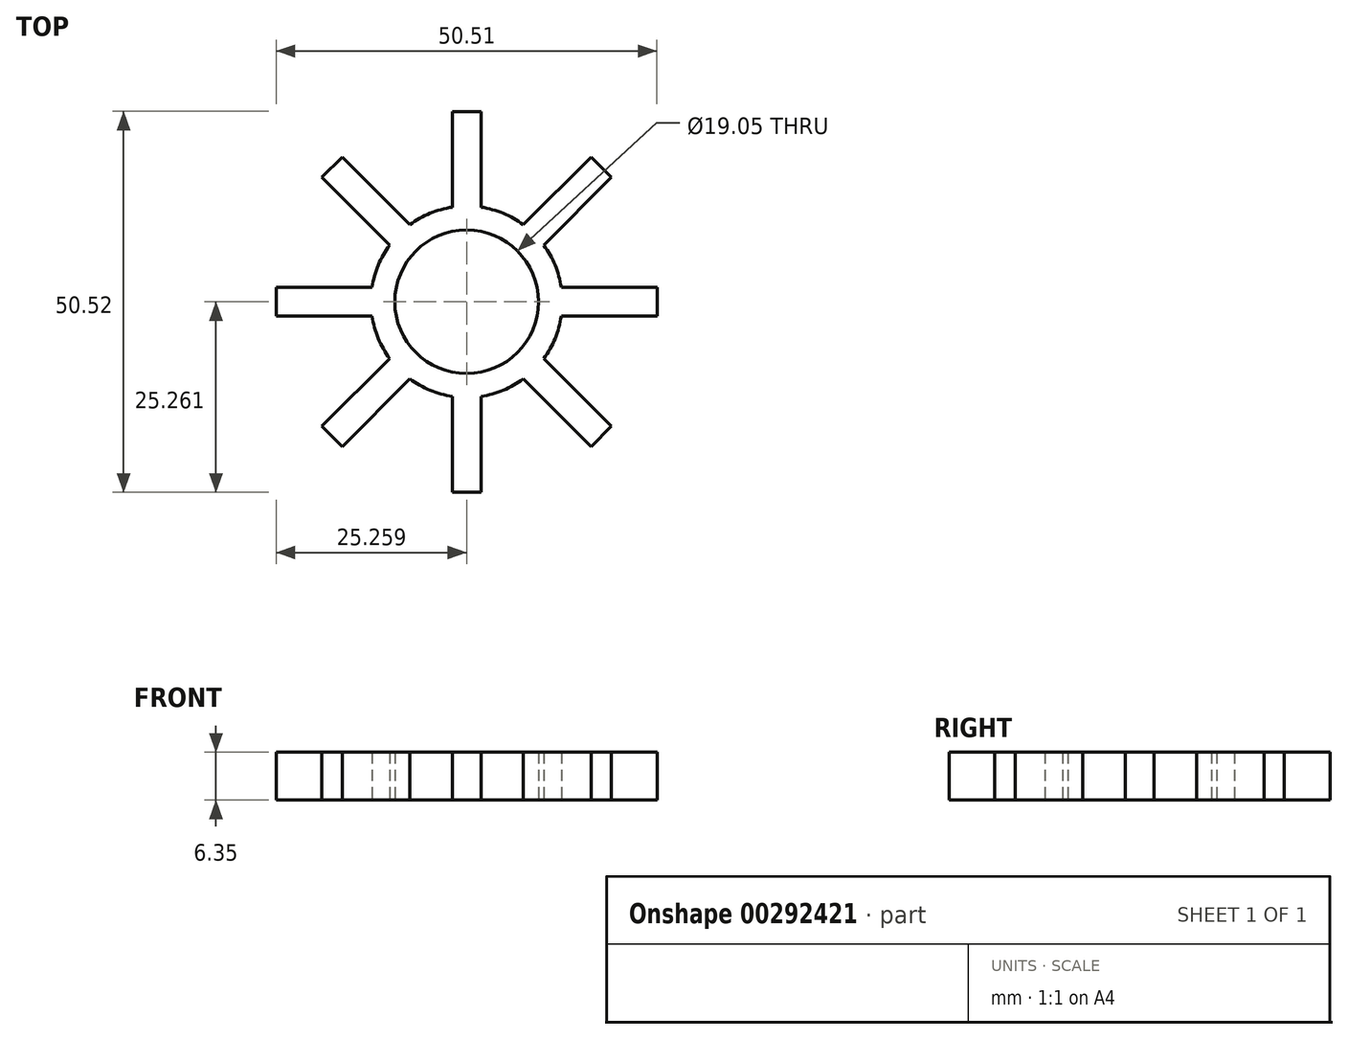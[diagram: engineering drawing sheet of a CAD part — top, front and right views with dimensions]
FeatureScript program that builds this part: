
annotation { "Feature Type Name" : "Feature", "Feature Type Description" : "" }
export const myFeature = defineFeature(function(context is Context, id is Id, definition is map)
    precondition{}
    {
        {
            var Q0;
            Q0=qCreatedBy(makeId("Top.planeOp"),FACE);
            var sketch = newSketch(context, id + "F0", { "sketchPlane" : qUnion([Q0])});
            skCircle(sketch, "E0", {"center": v(-10.94, 8.06) * mm, "radius": 9.53 * mm});
            skCircle(sketch, "E1", {"center": v(-10.94, 8.06) * mm, "radius": 12.7 * mm});
            skLineSegment(sketch, "E2.bottom", {"start": v(-12.85, 20.62) * mm, "end": v(-9.04, 20.62) * mm});
            skLineSegment(sketch, "E2.top", {"start": v(-12.85, 33.32) * mm, "end": v(-9.04, 33.32) * mm});
            skLineSegment(sketch, "E2.left", {"start": v(-12.85, 20.62) * mm, "end": v(-12.85, 33.32) * mm});
            skLineSegment(sketch, "E2.right", {"start": v(-9.04, 20.62) * mm, "end": v(-9.04, 33.32) * mm});
            skSolve(sketch);
        }
        {
            var Q0;
            Q0 = qSketchRegion(id + "F0", true);
            extrude(context, id + "F1", {"entities" : qUnion([Q0]), "depth" : 6.35 * mm, "offsetDistance" : 25.4 * mm});
        }
        {
            var Q0;
            Q0=makeQuery(id+"F1.opExtrude","SWEPT_BODY",BODY,{"disambiguationData":[OSD([sQuery(id+"F0.wireOp",EDGE,"E0"),sQuery(id+"F0.wireOp",EDGE,"E1"),sQuery(id+"F0.wireOp",EDGE,"E2.top"),sQuery(id+"F0.wireOp",EDGE,"E2.left"),sQuery(id+"F0.wireOp",EDGE,"E2.right")])]});
            var Q1;
            Q1=makeQuery(id+"F1.opExtrude","CAP_EDGE",EDGE,{"disambiguationData":[OSD([sQuery(id+"F0.wireOp",EDGE,"E0")])],"isStart":false});
            circularPattern(context, id + "F2", {"operationType" : NewBodyOperationType.ADD, "entities" : qUnion([Q0]), "axis" : qUnion([Q1]), "angle" : 360 * degree, "instanceCount" : 8, "equalSpace" : true});
        }
    });
